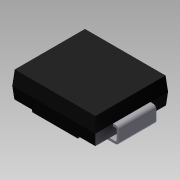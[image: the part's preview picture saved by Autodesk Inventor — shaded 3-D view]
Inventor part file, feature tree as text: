
AUTODESK INVENTOR PART (.ipt)
format: ipt  version: 2011 (Build 150239000, 239)  size: 194,560 bytes
history: native  units: mm
features: other x8, projected_geometry x5, extrude x4, sketch x4, mirror x1
ambient origin geometry x8: Origin, YZ Plane, XZ Plane, XY Plane, X Axis, Y Axis, Z Axis, Center Point
feature tree (22):
  other  "Твердое тело1"
  extrude  "Выдавливание1"  Depth=3.555mm
  extrude  "Выдавливание3"  Depth=3.11mm
  other  "РабПлоскость1"
  extrude  "Выдавливание4"  Depth=7.11mm
  other  "РабПлоскость10"
  extrude  "Выдавливание6"  Depth=6.22mm
  other  "РабПлоскость13"
  mirror  "Зеркальное отражение2"
  sketch  "Эскиз1"
  sketch  "Эскиз4"
  sketch  "Эскиз5"
  projected_geometry  "Спроецированная петля1"
  projected_geometry  "Спроецированная петля2"
  projected_geometry  "Спроецированная петля3"
  other  "РабПлоскость8"
  other  "РабПлоскость9"
  sketch  "Эскиз7"
  projected_geometry  "Спроецированная петля6"
  projected_geometry  "Спроецированная петля7"
  other  "РабПлоскость11"
  other  "РабПлоскость12"
